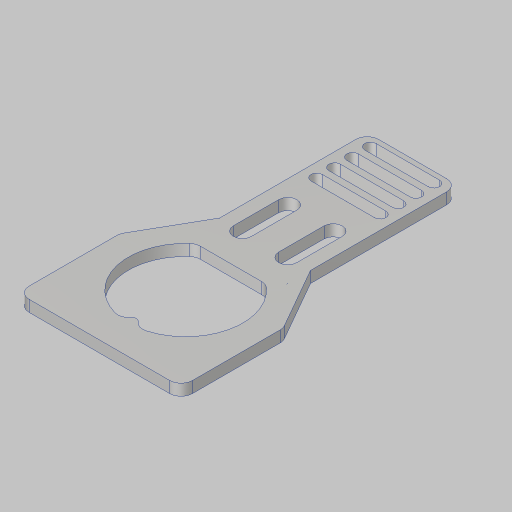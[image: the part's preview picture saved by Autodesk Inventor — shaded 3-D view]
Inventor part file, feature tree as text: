
AUTODESK INVENTOR PART (.ipt)
format: ipt  version: 2023.5 (Build 275446000, 446)  size: 262,656 bytes
history: native  units: in
note: dims shown in document units (in); Inventor stores cm internally (conversion verified against a paired STEP export)
features: sketch x5, extrude x5, fillet x4, projected_geometry x4
ambient origin geometry x8: Origin, YZ Plane, XZ Plane, XY Plane, X Axis, Y Axis, Z Axis, Center Point
bodies: Solid1 (feature_tree)
feature tree (18):
  sketch  "Sketch1"  dims[d1=0.7in d3=0.125in d4=0.197in]
  extrude  "Extrusion1"  Depth=0.125in
  fillet  "Fillet1"  Radius=0.197in
  extrude  "Extrusion2"  Depth=1.0in
  extrude  "Extrusion3"  Depth=0.25in
  fillet  "Fillet2"  Radius=0.5in
  extrude  "Extrusion4"  Depth=0.125in TaperAngle=0.0deg
  fillet  "Fillet3"  Radius=0.125in
  extrude  "Extrusion5"  Depth=0.5in
  fillet  "Fillet4"  Radius=1.375in
  sketch  "Sketch2"  dims[d5=0.197in d8=1.0in]
  sketch  "Sketch3"  dims[d9=2.0in d10=0.25in d11=0.5in]
  sketch  "Sketch4"  dims[d12=0.25in d13=0.125in d14=0.0in d22=0.125in]
  sketch  "Sketch5"  dims[d23=0.201in d24=0.5in d26=1.375in d27=0.5in d28=1.0in d29=0.0in d30=1.26in d31=0.5in d32=0.125in d33=1.0in d34=0.0in d35=0.125in d36=0.093in d37=0.042in d38=1.0in d39=0.0in d40=0.125in d41=0.7874in d43=0.197in d44=0.3937in d46=1.0in d48=1.8in d49=3.45in d50=1.125in d51=1.0in d52=0.0in d53=0.125in]
  projected_geometry  "Project Cut Edges1"
  projected_geometry  "Project Cut Edges2"
  projected_geometry  "Project Cut Edges3"
  projected_geometry  "Project Cut Edges4"
